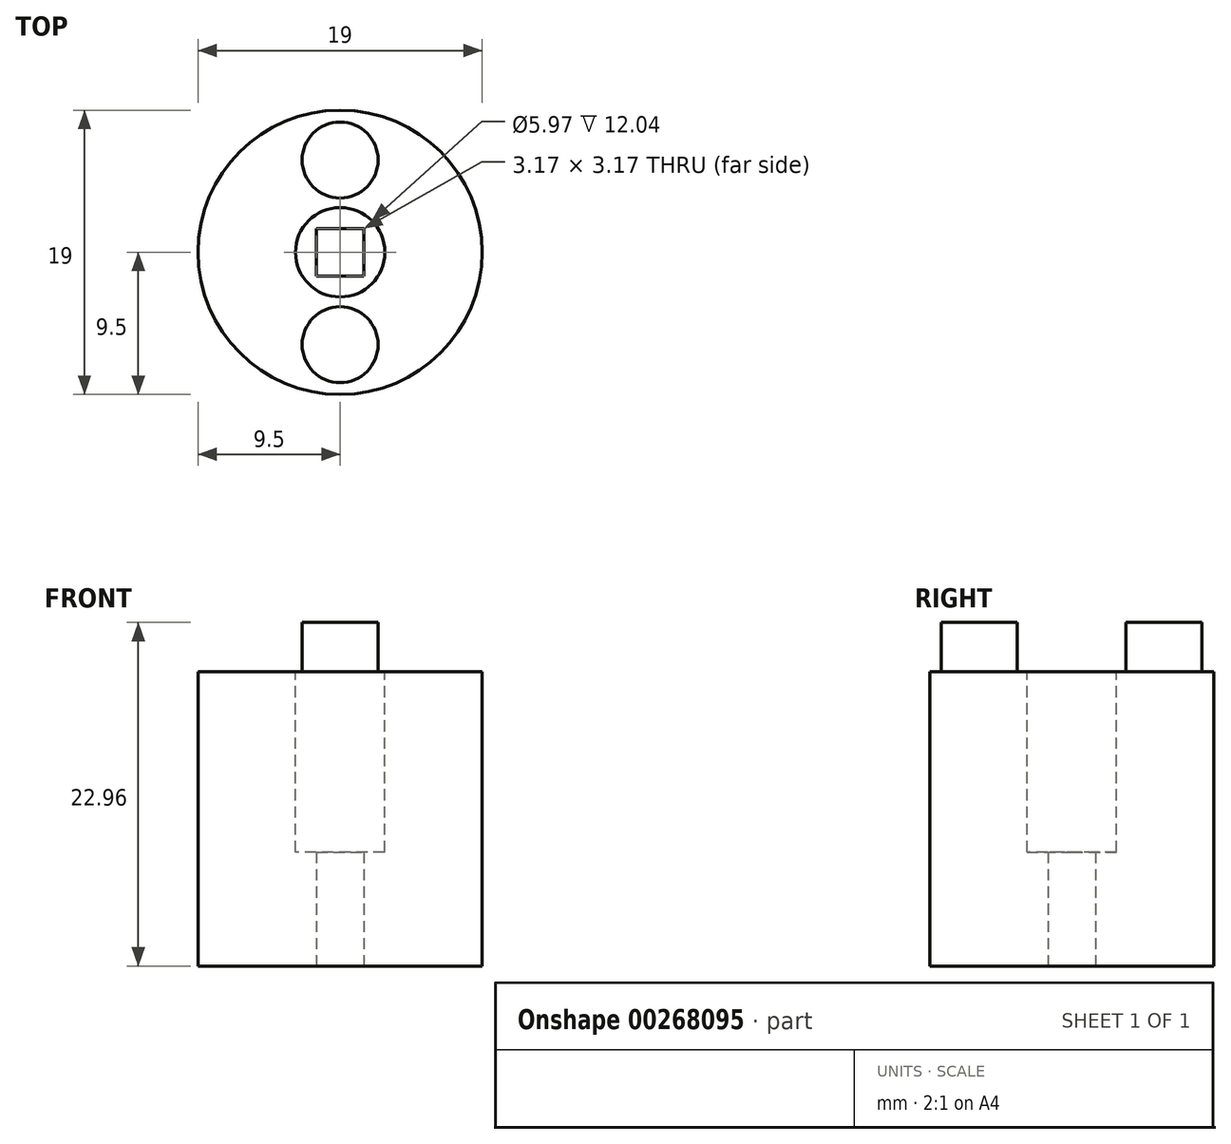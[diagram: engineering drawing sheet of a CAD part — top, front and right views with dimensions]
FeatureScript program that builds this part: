
annotation { "Feature Type Name" : "Feature", "Feature Type Description" : "" }
export const myFeature = defineFeature(function(context is Context, id is Id, definition is map)
    precondition{}
    {
        {
            var Q0;
            Q0=qCreatedBy(makeId("Top.planeOp"),FACE);
            var sketch = newSketch(context, id + "F0", { "sketchPlane" : qUnion([Q0])});
            skCircle(sketch, "E0", {"center": v(0, 0) * mm, "radius": 9.5 * mm});
            skSolve(sketch);
        }
        {
            var Q0;
            Q0 = qSketchRegion(id + "F0", true);
            extrude(context, id + "F1", {"entities" : qUnion([Q0]), "depth" : 19.66 * mm});
        }
        {
            var Q0;
            Q0=makeQuery(id+"F1.opExtrude","CAP_FACE",FACE,{"disambiguationData":[OSD([sQuery(id+"F0.wireOp",EDGE,"E0")])],"isStart":false});
            var sketch = newSketch(context, id + "F2", { "sketchPlane" : qUnion([Q0])});
            skCircle(sketch, "E1", {"center": v(0, 0) * mm, "radius": 2.98 * mm});
            skSolve(sketch);
        }
        {
            var Q0;
            Q0 = qSketchRegion(id + "F2", true);
            extrude(context, id + "F3", {"entities" : qUnion([Q0]), "operationType" : NewBodyOperationType.REMOVE, "oppositeDirection" : true, "depth" : 12.04 * mm});
        }
        {
            var Q0;
            Q0=makeQuery(id+"F1.opExtrude","CAP_FACE",FACE,{"disambiguationData":[OSD([sQuery(id+"F0.wireOp",EDGE,"E0")])],"isStart":false});
            var sketch = newSketch(context, id + "F4", { "sketchPlane" : qUnion([Q0])});
            skCircle(sketch, "E2", {"center": v(0, -6.17) * mm, "radius": 2.54 * mm});
            skCircle(sketch, "E3.MirrorC", {"center": v(0, 6.17) * mm, "radius": 2.54 * mm});
            skSolve(sketch);
        }
        {
            var Q0;
            Q0 = qSketchRegion(id + "F4", true);
            extrude(context, id + "F5", {"entities" : qUnion([Q0]), "operationType" : NewBodyOperationType.ADD, "depth" : 3.3 * mm});
        }
        {
            var Q0;
            Q0=makeQuery(id+"F1.opExtrude","CAP_FACE",FACE,{"disambiguationData":[OSD([sQuery(id+"F0.wireOp",EDGE,"E0")])],"isStart":true});
            var sketch = newSketch(context, id + "F6", { "sketchPlane" : qUnion([Q0])});
            skLineSegment(sketch, "E4.bottom", {"start": v(1.59, 1.59) * mm, "end": v(-1.59, 1.59) * mm});
            skLineSegment(sketch, "E4.top", {"start": v(1.59, -1.59) * mm, "end": v(-1.59, -1.59) * mm});
            skLineSegment(sketch, "E4.left", {"start": v(1.59, 1.59) * mm, "end": v(1.59, -1.59) * mm});
            skLineSegment(sketch, "E4.right", {"start": v(-1.59, 1.59) * mm, "end": v(-1.59, -1.59) * mm});
            skPoint(sketch, "E4.middle", {"position": v(0, 0) * mm});
            skSolve(sketch);
        }
        {
            var Q0;
            Q0 = qSketchRegion(id + "F6", true);
            extrude(context, id + "F7", {"entities" : qUnion([Q0]), "operationType" : NewBodyOperationType.REMOVE, "oppositeDirection" : true, "depth" : 25.4 * mm});
        }
    });
